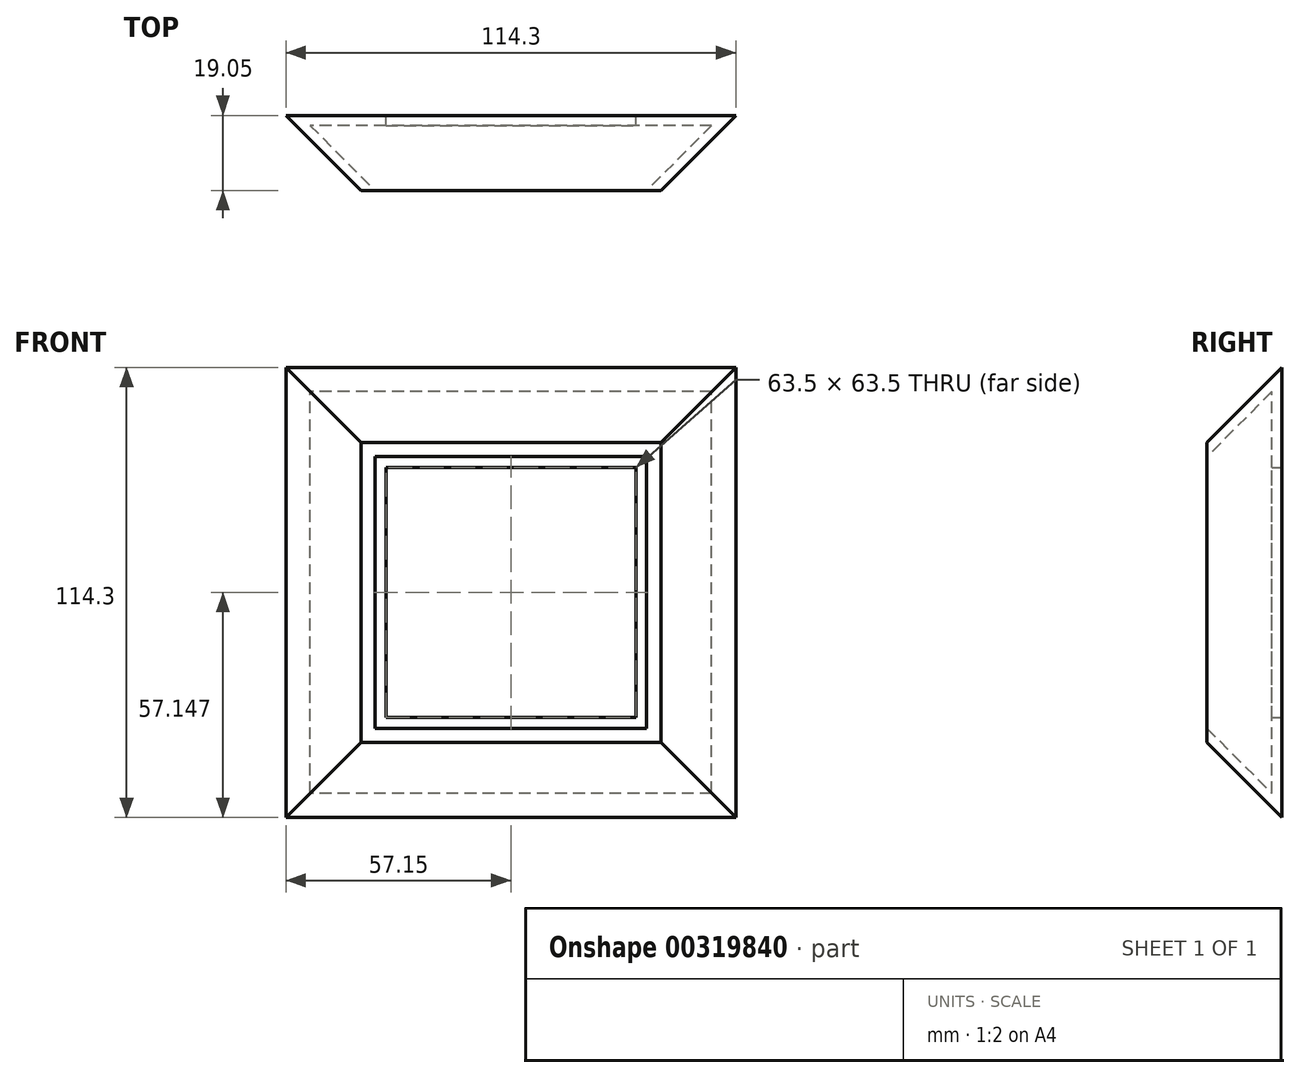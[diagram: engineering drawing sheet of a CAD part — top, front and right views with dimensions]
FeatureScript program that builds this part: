
annotation { "Feature Type Name" : "Feature", "Feature Type Description" : "" }
export const myFeature = defineFeature(function(context is Context, id is Id, definition is map)
    precondition{}
    {
        {
            var Q0;
            Q0=qCreatedBy(makeId("Front.planeOp"),FACE);
            var sketch = newSketch(context, id + "F0", { "sketchPlane" : qUnion([Q0])});
            skLineSegment(sketch, "E0.bottom", {"start": v(-115.1, 109.19) * mm, "end": v(11.9, 109.19) * mm});
            skLineSegment(sketch, "E0.top", {"start": v(-115.1, -17.81) * mm, "end": v(11.9, -17.81) * mm});
            skLineSegment(sketch, "E0.left", {"start": v(-115.1, 109.19) * mm, "end": v(-115.1, -17.81) * mm});
            skLineSegment(sketch, "E0.right", {"start": v(11.9, 109.19) * mm, "end": v(11.9, -17.81) * mm});
            skSolve(sketch);
        }
        {
            var Q0;
            Q0 = qSketchRegion(id + "F0", true);
            extrude(context, id + "F1", {"entities" : qUnion([Q0]), "depth" : 19.05 * mm});
        }
        {
            var Q0;
            Q0=makeQuery(id+"F1.opExtrude","CAP_FACE",FACE,{"disambiguationData":[OSD([sQuery(id+"F0.wireOp",EDGE,"E0.bottom"),sQuery(id+"F0.wireOp",EDGE,"E0.top"),sQuery(id+"F0.wireOp",EDGE,"E0.left"),sQuery(id+"F0.wireOp",EDGE,"E0.right")])],"isStart":false});
            chamfer(context, id + "F2", {"entities" : qUnion([Q0]), "width" : 25.4 * mm, "tangentPropagation" : true});
        }
        {
            var Q0;
            Q0=makeQuery(id+"F1.opExtrude","CAP_FACE",FACE,{"disambiguationData":[OSD([sQuery(id+"F0.wireOp",EDGE,"E0.bottom"),sQuery(id+"F0.wireOp",EDGE,"E0.top"),sQuery(id+"F0.wireOp",EDGE,"E0.left"),sQuery(id+"F0.wireOp",EDGE,"E0.right")])],"isStart":false});
            shell(context, id + "F3", {"entities" : qUnion([Q0]), "thickness" : 2.54 * mm});
        }
        {
            var Q0;
            Q0=makeQuery(id+"F1.opExtrude","CAP_FACE",FACE,{"disambiguationData":[OSD([sQuery(id+"F0.wireOp",EDGE,"E0.bottom"),sQuery(id+"F0.wireOp",EDGE,"E0.top"),sQuery(id+"F0.wireOp",EDGE,"E0.left"),sQuery(id+"F0.wireOp",EDGE,"E0.right")])],"isStart":true});
            var sketch = newSketch(context, id + "F4", { "sketchPlane" : qUnion([Q0])});
            skLineSegment(sketch, "E1.bottom", {"start": v(19.85, 77.44) * mm, "end": v(83.35, 77.44) * mm});
            skLineSegment(sketch, "E1.top", {"start": v(19.85, 13.94) * mm, "end": v(83.35, 13.94) * mm});
            skLineSegment(sketch, "E1.left", {"start": v(19.85, 77.44) * mm, "end": v(19.85, 13.94) * mm});
            skLineSegment(sketch, "E1.right", {"start": v(83.35, 77.44) * mm, "end": v(83.35, 13.94) * mm});
            skSolve(sketch);
        }
        {
            var Q0;
            Q0 = qSketchRegion(id + "F4", true);
            extrude(context, id + "F5", {"entities" : qUnion([Q0]), "operationType" : NewBodyOperationType.REMOVE, "oppositeDirection" : true, "depth" : 25.4 * mm});
        }
    });
